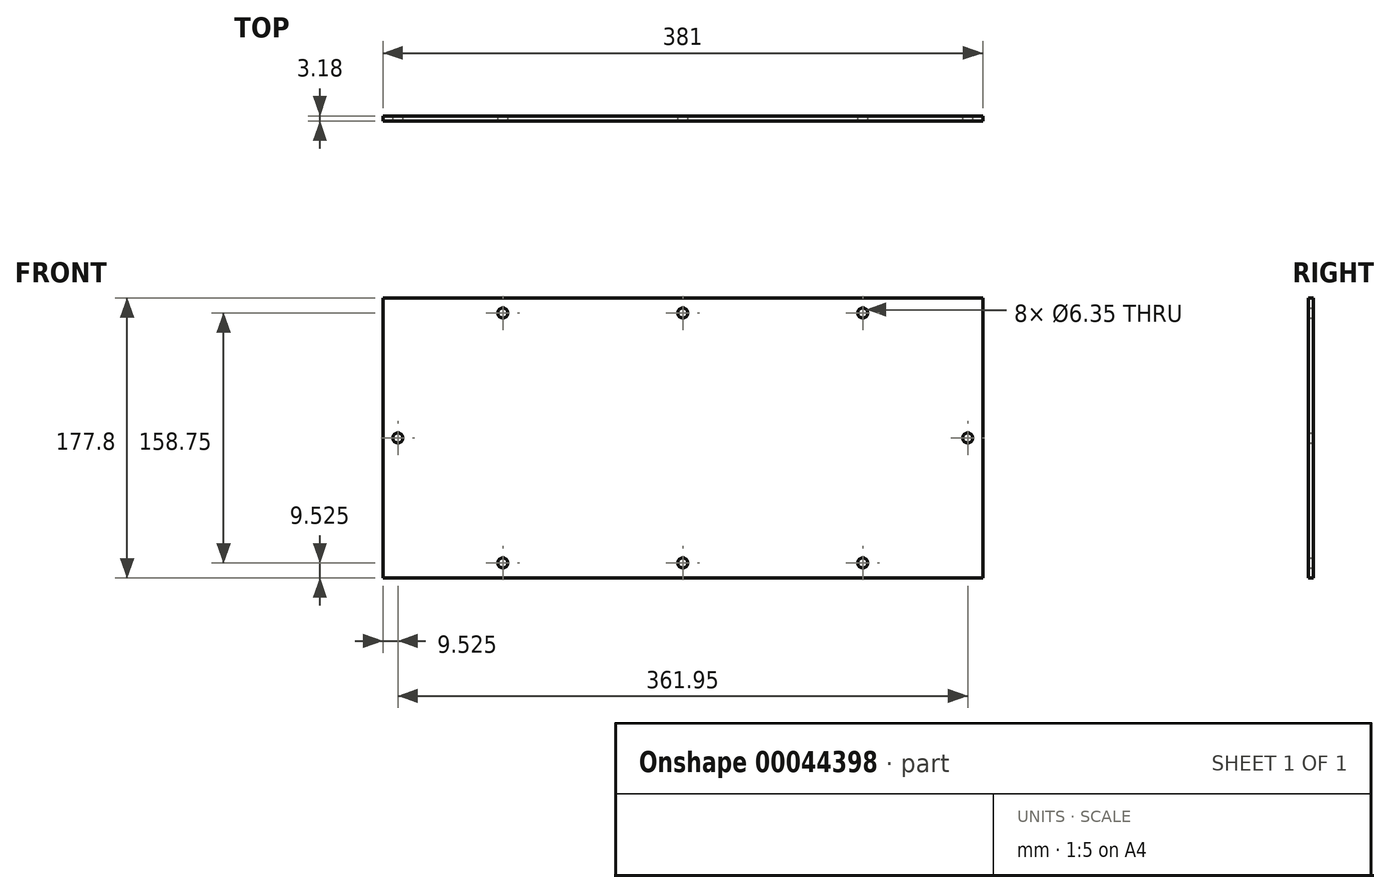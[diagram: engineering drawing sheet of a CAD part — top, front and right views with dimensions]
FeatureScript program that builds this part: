
annotation { "Feature Type Name" : "Feature", "Feature Type Description" : "" }
export const myFeature = defineFeature(function(context is Context, id is Id, definition is map)
    precondition{}
    {
        {
            var Q0;
            Q0=qCreatedBy(makeId("Front.planeOp"),FACE);
            var sketch = newSketch(context, id + "F0", { "sketchPlane" : qUnion([Q0])});
            skLineSegment(sketch, "E0.rect.bottom", {"start": v(190.5, 88.9) * mm, "end": v(-190.5, 88.9) * mm});
            skLineSegment(sketch, "E0.rect.top", {"start": v(190.5, -88.9) * mm, "end": v(-190.5, -88.9) * mm});
            skLineSegment(sketch, "E0.rect.left", {"start": v(190.5, 88.9) * mm, "end": v(190.5, -88.9) * mm});
            skLineSegment(sketch, "E0.rect.right", {"start": v(-190.5, 88.9) * mm, "end": v(-190.5, -88.9) * mm});
            skPoint(sketch, "E0.rect.middle", {"position": v(0, 0) * mm});
            skPoint(sketch, "E1", {"position": v(-190.5, 0) * mm});
            skPoint(sketch, "E2", {"position": v(0, 88.9) * mm});
            skLineSegment(sketch, "E3", {"start": v(0, 109.45) * mm, "end": v(0, -107.19) * mm, "construction": true});
            skLineSegment(sketch, "E4", {"start": v(-199.2, 0) * mm, "end": v(219.92, 0) * mm, "construction": true});
            skPoint(sketch, "E5", {"position": v(-114.3, 88.9) * mm});
            skPoint(sketch, "E6", {"position": v(114.3, 88.9) * mm});
            skCircle(sketch, "E7", {"center": v(-180.97, 0) * mm, "radius": 3.18 * mm});
            skCircle(sketch, "E8", {"center": v(180.98, 0) * mm, "radius": 3.18 * mm});
            skCircle(sketch, "E9", {"center": v(114.3, 79.38) * mm, "radius": 3.18 * mm});
            skCircle(sketch, "E10", {"center": v(0, 79.38) * mm, "radius": 3.18 * mm});
            skCircle(sketch, "E11", {"center": v(-114.3, 79.38) * mm, "radius": 3.18 * mm});
            skCircle(sketch, "E12", {"center": v(-114.3, -79.37) * mm, "radius": 3.18 * mm});
            skCircle(sketch, "E13", {"center": v(0, -79.38) * mm, "radius": 3.18 * mm});
            skCircle(sketch, "E14", {"center": v(114.3, -79.38) * mm, "radius": 3.18 * mm});
            skSolve(sketch);
        }
        {
            var Q0;
            Q0=makeQuery(id+"F0.imprint","IMPRINT",FACE,{"disambiguationData":[TD([[makeQuery(id+"F0.imprint","IMPRINT",EDGE,{"derivedFrom":sQuery(id+"F0.wireOp",EDGE,"E0.rect.bottom")}),1.0]])]});
            extrude(context, id + "F1", {"entities" : qUnion([Q0]), "depth" : 3.17 * mm});
        }
    });
